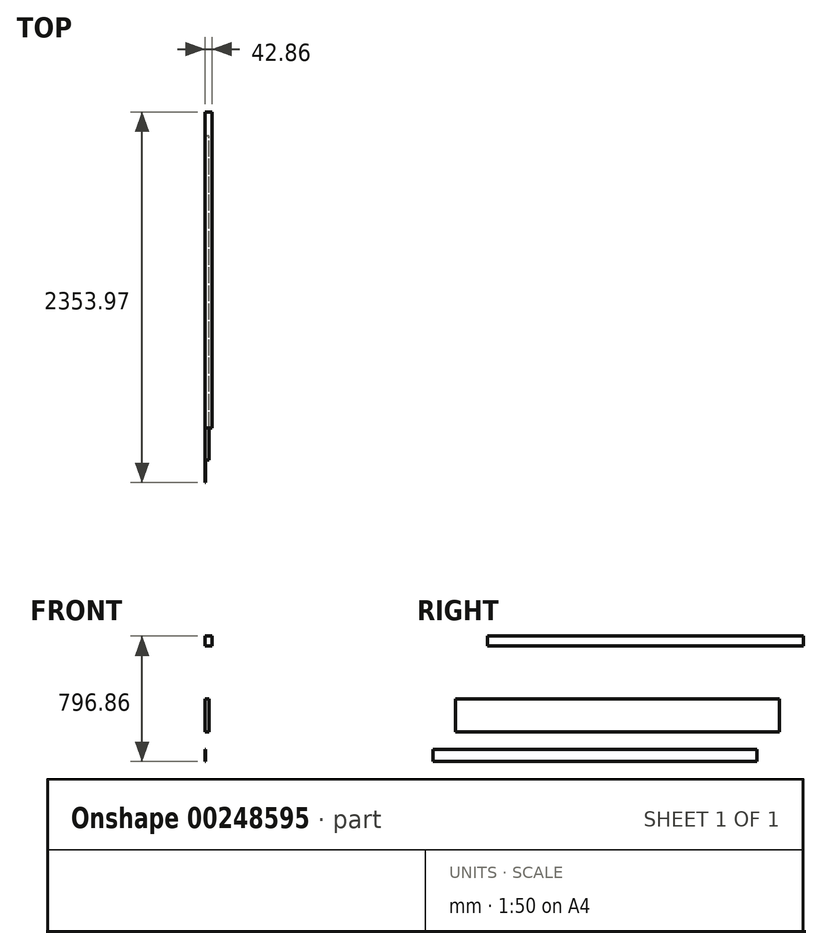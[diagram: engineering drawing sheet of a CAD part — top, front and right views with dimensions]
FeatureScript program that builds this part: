
annotation { "Feature Type Name" : "Feature", "Feature Type Description" : "" }
export const myFeature = defineFeature(function(context is Context, id is Id, definition is map)
    precondition{}
    {
        {
            var Q0;
            Q0=qCreatedBy(makeId("Right.planeOp"),FACE);
            var sketch = newSketch(context, id + "F0", { "sketchPlane" : qUnion([Q0])});
            skLineSegment(sketch, "E0.bottom", {"start": v(-1224.38, -496.65) * mm, "end": v(833.02, -496.65) * mm});
            skLineSegment(sketch, "E0.top", {"start": v(-1224.38, -572.85) * mm, "end": v(833.02, -572.85) * mm});
            skLineSegment(sketch, "E0.left", {"start": v(-1224.38, -496.65) * mm, "end": v(-1224.38, -572.85) * mm});
            skLineSegment(sketch, "E0.right", {"start": v(833.02, -496.65) * mm, "end": v(833.02, -572.85) * mm});
            skSolve(sketch);
        }
        {
            var Q0;
            Q0=makeQuery(id+"F0.imprint","IMPRINT",FACE,{"disambiguationData":[TD([[makeQuery(id+"F0.imprint","IMPRINT",EDGE,{"derivedFrom":sQuery(id+"F0.wireOp",EDGE,"E0.bottom")}),-1.0]])]});
            extrude(context, id + "F1", {"entities" : qUnion([Q0]), "depth" : (1 + (11 / 16)) * mm});
        }
        {
            var Q0;
            Q0=qCreatedBy(makeId("Right.planeOp"),FACE);
            var sketch = newSketch(context, id + "F2", { "sketchPlane" : qUnion([Q0])});
            skLineSegment(sketch, "E1.bottom", {"start": v(-1081.07, -173.85) * mm, "end": v(976.33, -173.85) * mm});
            skLineSegment(sketch, "E1.top", {"start": v(-1081.07, -384.99) * mm, "end": v(976.33, -384.99) * mm});
            skLineSegment(sketch, "E1.left", {"start": v(-1081.07, -173.85) * mm, "end": v(-1081.07, -384.99) * mm});
            skLineSegment(sketch, "E1.right", {"start": v(976.33, -173.85) * mm, "end": v(976.33, -384.99) * mm});
            skSolve(sketch);
        }
        {
            var Q0;
            Q0=makeQuery(id+"F2.imprint","IMPRINT",FACE,{"disambiguationData":[TD([[makeQuery(id+"F2.imprint","IMPRINT",EDGE,{"derivedFrom":sQuery(id+"F2.wireOp",EDGE,"E1.bottom")}),-1.0]])]});
            extrude(context, id + "F3", {"entities" : qUnion([Q0]), "depth" : 25.4 * mm});
        }
        {
            var Q0;
            Q0=qCreatedBy(makeId("Right.planeOp"),FACE);
            var sketch = newSketch(context, id + "F4", { "sketchPlane" : qUnion([Q0])});
            skLineSegment(sketch, "E2.bottom", {"start": v(-877, 224) * mm, "end": v(1129.6, 224) * mm});
            skLineSegment(sketch, "E2.top", {"start": v(-877, 160.5) * mm, "end": v(1129.6, 160.5) * mm});
            skLineSegment(sketch, "E2.left", {"start": v(-877, 224) * mm, "end": v(-877, 160.5) * mm});
            skLineSegment(sketch, "E2.right", {"start": v(1129.6, 224) * mm, "end": v(1129.6, 160.5) * mm});
            skSolve(sketch);
        }
        {
            var Q0;
            Q0=makeQuery(id+"F4.imprint","IMPRINT",FACE,{"disambiguationData":[TD([[makeQuery(id+"F4.imprint","IMPRINT",EDGE,{"derivedFrom":sQuery(id+"F4.wireOp",EDGE,"E2.bottom")}),-1.0]])]});
            extrude(context, id + "F5", {"entities" : qUnion([Q0]), "depth" : 42.86 * mm});
        }
    });
